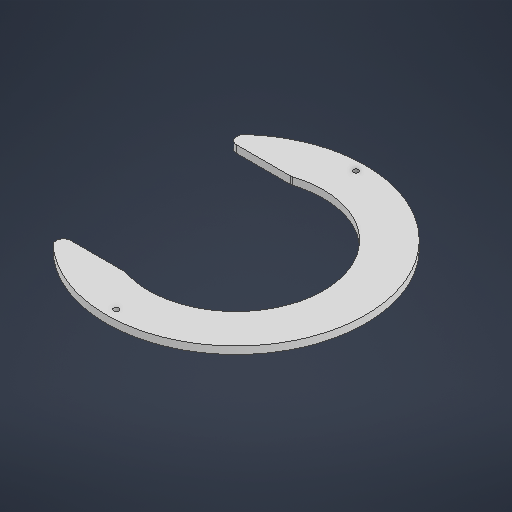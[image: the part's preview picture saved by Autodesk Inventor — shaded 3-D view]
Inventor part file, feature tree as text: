
AUTODESK INVENTOR PART (.ipt)
format: ipt  version: 2025 (Build 290162000, 162)  size: 220,160 bytes
history: native  units: in
note: dims shown in document units (in); Inventor stores cm internally (conversion verified against a paired STEP export)
features: extrude x1, fillet x1, sketch x1
ambient origin geometry x8: Origin, YZ Plane, XZ Plane, XY Plane, X Axis, Y Axis, Z Axis, Center Point
bodies: Solid1 (feature_tree)
feature tree (3):
  extrude  "Extrusion1"  Depth=0.1969in
  fillet  "Fillet1"  Radius=6.8898in
  sketch  "Sketch1"  dims[d0=4.6457in d1=6.378in d2=6.8898in d3=0.1378in d4=0.1378in d5=0.1969in d6=0.0in d7=4.4094in d9=3.1496in d10=0.3937in d11=0.1969in d12=0.1969in]
